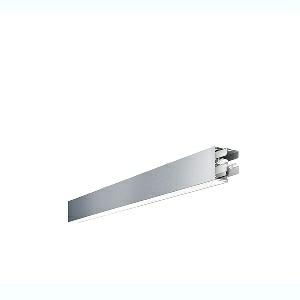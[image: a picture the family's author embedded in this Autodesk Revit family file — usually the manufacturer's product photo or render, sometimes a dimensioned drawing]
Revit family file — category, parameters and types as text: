
# Revit family: dotoo_line_-_dla_2000_840_d_mid_00807956_1012
name_source: partatom
category: Lighting Fixtures
units: mm (PartAtom-declared; Revit-internal decimal feet)

## family parameters
Cut with Voids When Loaded = No
Host = Face
Light Source = No
Part Type = Normal
Room Calculation Point = No
Round Connector Dimension = Use Diameter
Shared = No

## types (1)
- DOTOO.line - DLA 2000/840/D MID (1 x LED, 1700 lm, 4000K)
    Apparent Load = 16 VA
    Approval mark = CE
    CIE Flux Codes = 67 91 98 100 100
    Color Rendering = 80-89
    Color Temperature = 4000K
    Control Gear = Electronic ballast
    Default Elevation = 1800 mm
    Description = DLA 2000/840/D|Surface-mounted luminaire.|light source: LED|work equipment: Adjustable electronic ballast, digital DALI|connected load: 220-240 V, 50/60 Hz|Power consumption: approx. 16 W|luminous flux: 1700 lm|luminous efficacy: 106 lm/W|light distribution: Direct|colour temperature: Cold white, ca. 4000 K|class of protection: I|technology: Continuously dimmable|mains lead: Connector|glare control: Prism aperture|special features: DALI Load 1x, TouchDIM - dimming via standard switch, Through-wired, up to 18 m on one mains connection, Flicker-free, Suitable as emergency lighting, Mechanical and electrical connection of the individual modules without tools|
    Frequency = 50 Hz
    Height = 110 mm
    Lamp = 1 x LED
    Lamp Light Flux = 1700 lm
    Lamp count = 1
    Length = 1402 mm
    Luminous efficacy = 106 lm/W
    Manufacturer = Waldmann
    ModVariant = No
    Model = 00807956
    Mounting Place = Ceiling
    Mounting Type = Surface mounted
    Number of Poles = 1
    OnlyDefault = Yes
    Power Factor = 1
    Product Name = DOTOO.line - DLA 2000/840/D MID
    Product group = Ceiling mounted luminaire
    ProductGroupID = 3
    Protection Class = Protection class I
    Protection Degree = IP 40
    RLX_Detail_Level = 1
    RLX_Emergency_Light_Flux = 0 lm
    RLX_Emergency_Type = 0
    RLX_Emergency_Type_DB = No
    RlxData = <blob elided: 18137 chars, md5=add5dad2>
    Socket = socket
    Standby Power = 0 W
    System Light Flux = 1700 lm
    System Power = 16 W
    Type Comments = Product without accessories
    Type Image = 114373000-00807950.jpg
    URL = http://relux.com
    VarID = ---
    Voltage = 230 V
    Voltage Range = 220-240 V
    Weight = 0.00 kg
    Width = 60 mm  [stored 0.19685 ft]

note: [stored X ft] marks values corroborated as IEEE doubles in the binary element streams (Revit-internal decimal feet)

## geometry (parser evidence)
native form markers: Blend x4, Sweep x10
no freeform markers — native parametric forms only
